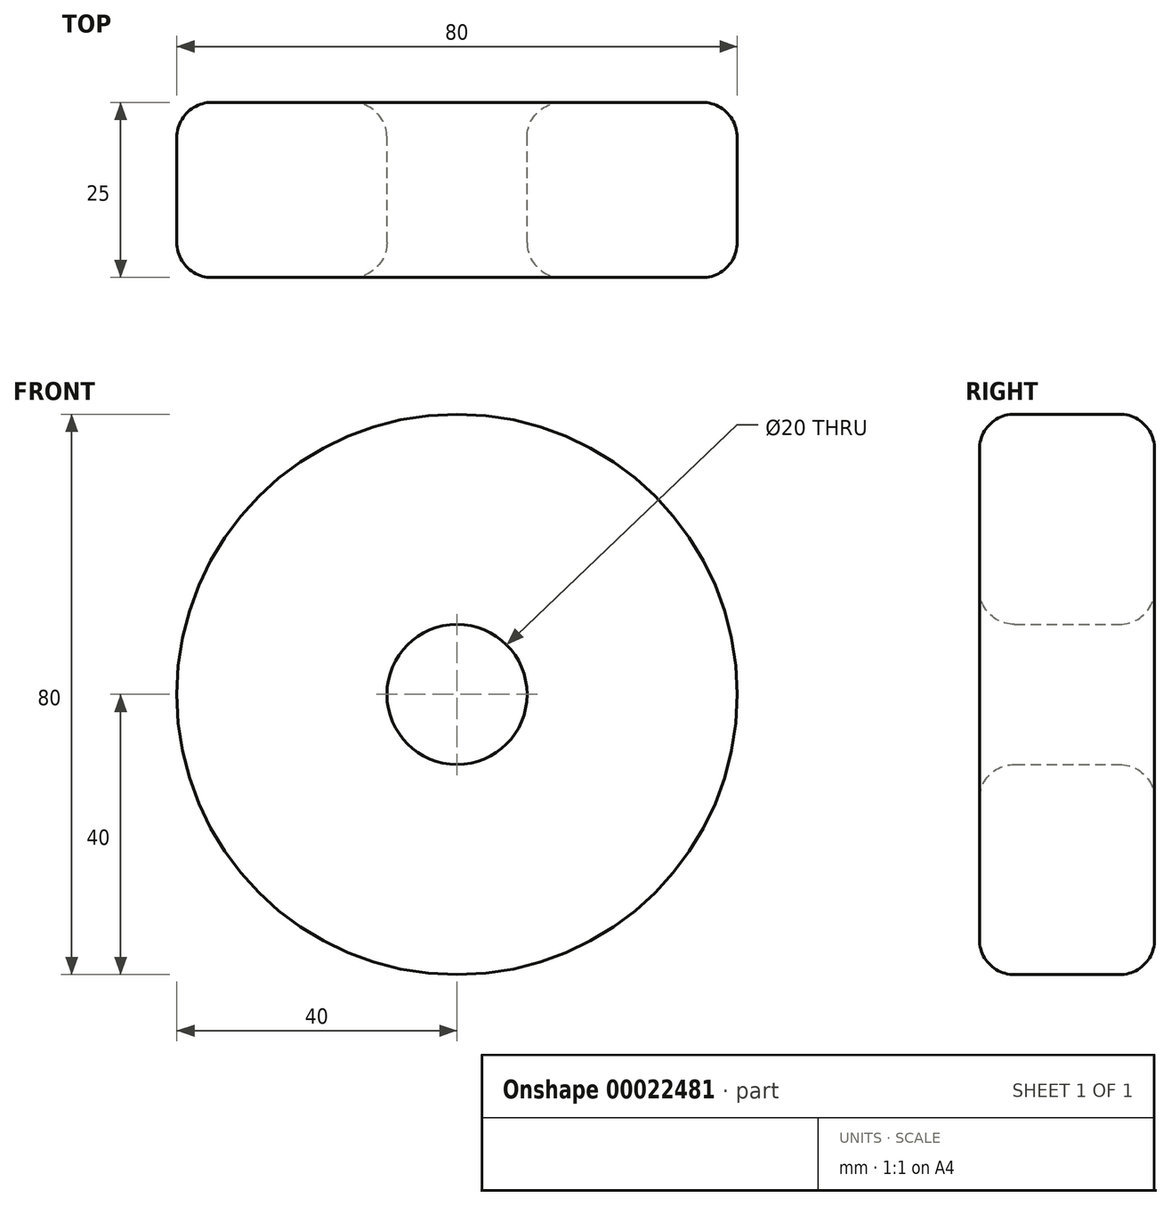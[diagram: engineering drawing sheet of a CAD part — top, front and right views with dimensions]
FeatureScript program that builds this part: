
annotation { "Feature Type Name" : "Feature", "Feature Type Description" : "" }
export const myFeature = defineFeature(function(context is Context, id is Id, definition is map)
    precondition{}
    {
        {
            var Q0;
            Q0=qCreatedBy(makeId("Front.planeOp"),FACE);
            var sketch = newSketch(context, id + "F0", { "sketchPlane" : qUnion([Q0])});
            skCircle(sketch, "E0", {"center": v(0, 0) * mm, "radius": 40 * mm});
            skCircle(sketch, "E1", {"center": v(0, 0) * mm, "radius": 10 * mm});
            skSolve(sketch);
        }
        {
            var Q0;
            Q0=makeQuery(id+"F0.imprint","IMPRINT",FACE,{"disambiguationData":[TD([[makeQuery(id+"F0.imprint","IMPRINT",EDGE,{"derivedFrom":sQuery(id+"F0.wireOp",EDGE,"E0")}),1.0]])]});
            extrude(context, id + "F1", {"entities" : qUnion([Q0]), "depth" : 25 * mm});
        }
        {
            var Q0;
            Q0=makeQuery(id+"F1.opExtrude","SWEPT_FACE",FACE,{"disambiguationData":[OSD([sQuery(id+"F0.wireOp",EDGE,"E1")])]});
            var Q1;
            Q1=makeQuery(id+"F1.opExtrude","CAP_EDGE",EDGE,{"disambiguationData":[OSD([sQuery(id+"F0.wireOp",EDGE,"E0")])],"isStart":true});
            var Q2;
            Q2=makeQuery(id+"F1.opExtrude","SWEPT_FACE",FACE,{"disambiguationData":[OSD([sQuery(id+"F0.wireOp",EDGE,"E0")])]});
            var Q3;
            Q3=makeQuery(id+"F1.opExtrude","CAP_EDGE",EDGE,{"disambiguationData":[OSD([sQuery(id+"F0.wireOp",EDGE,"E0")])],"isStart":false});
            var Q4;
            Q4=makeQuery(id+"F1.opExtrude","CAP_FACE",FACE,{"disambiguationData":[OSD([sQuery(id+"F0.wireOp",EDGE,"E0"),sQuery(id+"F0.wireOp",EDGE,"E1")])],"isStart":true});
            var Q5;
            Q5=makeQuery(id+"F1.opExtrude","CAP_FACE",FACE,{"disambiguationData":[OSD([sQuery(id+"F0.wireOp",EDGE,"E0"),sQuery(id+"F0.wireOp",EDGE,"E1")])],"isStart":false});
            var Q6;
            Q6=makeQuery(id+"F1.opExtrude","CAP_EDGE",EDGE,{"disambiguationData":[OSD([sQuery(id+"F0.wireOp",EDGE,"E1")])],"isStart":false});
            var Q7;
            Q7=makeQuery(id+"F1.opExtrude","CAP_EDGE",EDGE,{"disambiguationData":[OSD([sQuery(id+"F0.wireOp",EDGE,"E1")])],"isStart":true});
            fillet(context, id + "F2", {"entities" : qUnion([Q0, Q1, Q2, Q3, Q4, Q5, Q6, Q7]), "radius" : 5 * mm, "tangentPropagation" : true, "allowEdgeOverflow" : false});
        }
    });
